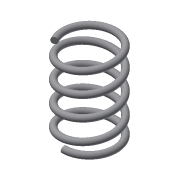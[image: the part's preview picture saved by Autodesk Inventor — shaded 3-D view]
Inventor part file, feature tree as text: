
AUTODESK INVENTOR PART (.ipt)
format: ipt  version: 2016 (Build 200138000, 138)  size: 357,376 bytes
history: native  units: mm
features: helix x1, revolve x1, sketch x1
ambient origin geometry x8: Origin, YZ Plane, XZ Plane, XY Plane, X Axis, Y Axis, Z Axis, Center Point
bodies: Body1 (feature_tree)
feature tree (3):
  helix  "Coil2"  [1 undecoded]
  revolve  "Revolution1"  [1 undecoded]
  sketch  "Sketch3"  dims[d15=5.0mm d16=3.0mm d17=15.0mm d18=35.0mm d19=0.0mm d20=90.0deg d21=150.0deg d22=90.0deg d23=150.0deg d24=0.032744mm d25=90.0deg]
note: 2 required parameter values undecoded (feature->parameter linkage not recoverable at this tier; creation-order binding heuristic only, values carry confidence <= 0.55)